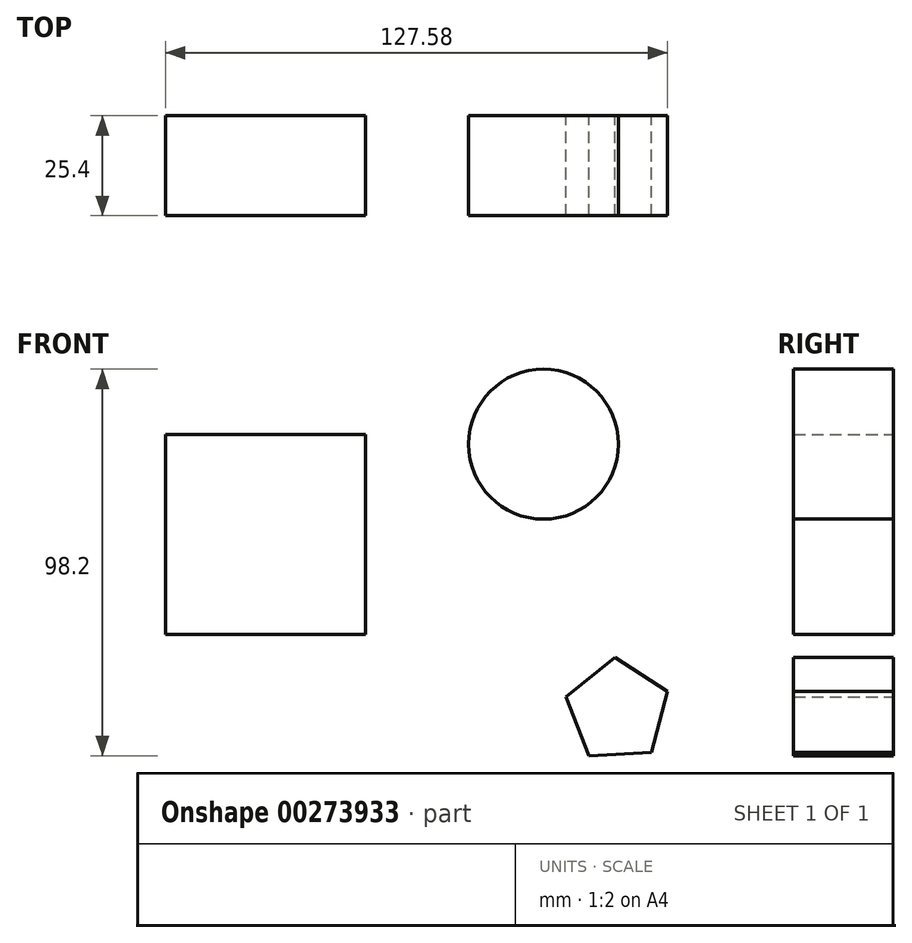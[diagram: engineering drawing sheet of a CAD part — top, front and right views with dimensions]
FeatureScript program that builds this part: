
annotation { "Feature Type Name" : "Feature", "Feature Type Description" : "" }
export const myFeature = defineFeature(function(context is Context, id is Id, definition is map)
    precondition{}
    {
        {
            var Q0;
            Q0=qCreatedBy(makeId("Front.planeOp"),FACE);
            var sketch = newSketch(context, id + "F0", { "sketchPlane" : qUnion([Q0])});
            skLineSegment(sketch, "E0.bottom", {"start": v(-50.8, 41.67) * mm, "end": v(0, 41.67) * mm});
            skLineSegment(sketch, "E0.top", {"start": v(-50.8, -9.13) * mm, "end": v(0, -9.13) * mm});
            skLineSegment(sketch, "E0.left", {"start": v(-50.8, 41.67) * mm, "end": v(-50.8, -9.13) * mm});
            skLineSegment(sketch, "E0.right", {"start": v(0, 41.67) * mm, "end": v(0, -9.13) * mm});
            skCircle(sketch, "E1", {"center": v(45.24, 39.16) * mm, "radius": 19.05 * mm});
            skCircle(sketch, "E2.cCircle", {"center": v(64.11, -28.57) * mm, "radius": 13.59 * mm, "construction": true});
            skLineSegment(sketch, "E2.0", {"start": v(76.78, -23.65) * mm, "end": v(72.7, -39.1) * mm});
            skLineSegment(sketch, "E2.1", {"start": v(72.7, -39.1) * mm, "end": v(56.75, -39.99) * mm});
            skLineSegment(sketch, "E2.2", {"start": v(56.75, -39.99) * mm, "end": v(50.98, -25.1) * mm});
            skLineSegment(sketch, "E2.3", {"start": v(50.98, -25.1) * mm, "end": v(63.35, -15) * mm});
            skLineSegment(sketch, "E2.4", {"start": v(63.35, -15) * mm, "end": v(76.78, -23.65) * mm});
            skSolve(sketch);
        }
        {
            var Q0;
            Q0 = qSketchRegion(id + "F0", true);
            extrude(context, id + "F1", {"entities" : qUnion([Q0]), "depth" : 25.4 * mm});
        }
    });
